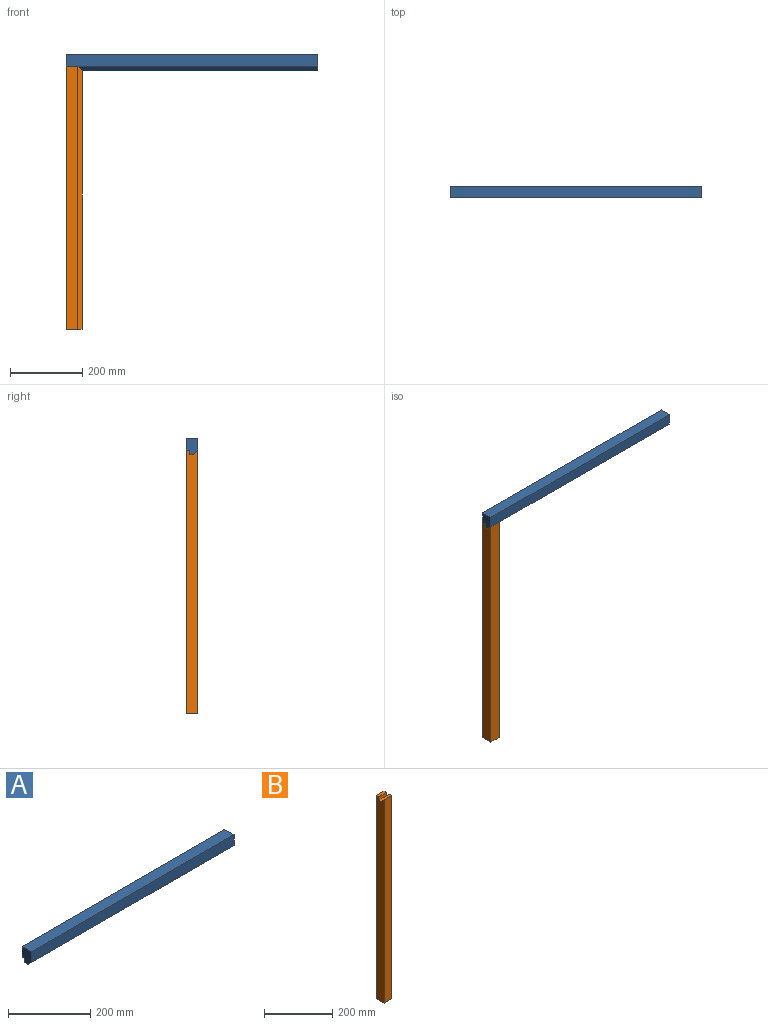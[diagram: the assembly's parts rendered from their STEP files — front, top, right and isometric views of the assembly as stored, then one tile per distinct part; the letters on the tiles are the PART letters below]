
ASSEMBLY  parts=2 mates=1
PART A: 9 faces, bbox 698.5x31.8x44.5 mm
  f0: plane 44.45x31.75mm, normal (-1,0,0), area 1209.7mm2, adj f1,f2,f3,f5,f6,f7,f8
  f1: plane 698.5x31.75mm, normal (0,1,0), area 22177.4mm2, adj f0,f2,f4,f7
  f2: plane 698.5x31.75mm, normal (0,0,1), area 22177.4mm2, adj f0,f1,f4,f5
  f3: plane 698.5x9.53mm, normal (0,0,-1), area 6653.2mm2, adj f0,f4,f6,f8
  f4: plane 44.45x31.75mm, normal (1,0,0), area 1209.7mm2, adj f1,f2,f3,f5,f6,f7,f8
  f5: plane 698.5x31.75mm, normal (0,-1,0), area 22177.4mm2, adj f0,f2,f4,f6
  f6: plane 698.5x12.7mm, normal (0,-0.71,-0.71), area 12545.4mm2, adj f0,f3,f4,f5
  f7: plane 698.5x9.53mm, normal (0,0,-1), area 6653.2mm2, adj f0,f1,f4,f8
  f8: plane 698.5x12.7mm, normal (0,1,0), area 8871mm2, adj f0,f3,f4,f7
PART B: 12 faces, bbox 44.5x31.8x730.3 mm
  f0: plane 730.25x31.75mm, normal (0,1,0), area 23185.4mm2, adj f3,f4,f7,f9
  f1: plane 730.25x31.75mm, normal (0,-1,0), area 23185.4mm2, adj f3,f4,f5,f11
  f2: plane 717.55x9.53mm, normal (1,0,0), area 6834.7mm2, adj f4,f5,f6,f10
  f3: plane 730.25x31.75mm, normal (-1,0,0), area 22983.8mm2, adj f0,f1,f4,f8,f9,f10,f11
  f4: plane 44.45x31.75mm, normal (0,0,-1), area 1209.7mm2, adj f0,f1,f2,f3,f5,f6,f7
  f5: plane 730.25x12.7mm, normal (0.71,-0.71,0), area 13001.6mm2, adj f1,f2,f4,f11
  f6: plane 717.55x12.7mm, normal (0,1,0), area 9112.9mm2, adj f2,f4,f7,f10
  f7: plane 730.25x9.53mm, normal (1,0,0), area 6955.6mm2, adj f0,f4,f6,f8,f9
  f8: plane 31.75x12.7mm, normal (0,-1,0), area 403.2mm2, adj f3,f7,f9,f10
  f9: plane 31.75x9.53mm, normal (0,0,1), area 302.4mm2, adj f0,f3,f7,f8
  f10: plane 44.45x9.53mm, normal (0,0,1), area 423.4mm2, adj f2,f3,f6,f8,f11
  f11: plane 44.45x12.7mm, normal (0,0.71,0.71), area 684.3mm2, adj f1,f3,f5,f10
PLACE A t=(-147.5,224.24,-750.94)mm
PLACE B t=(-173.5,224.24,-528.69)mm
MATE fastened A.f7 <-> B.f9  axis (0,0,-1) through (-317.91,224.24,105.18)mm
